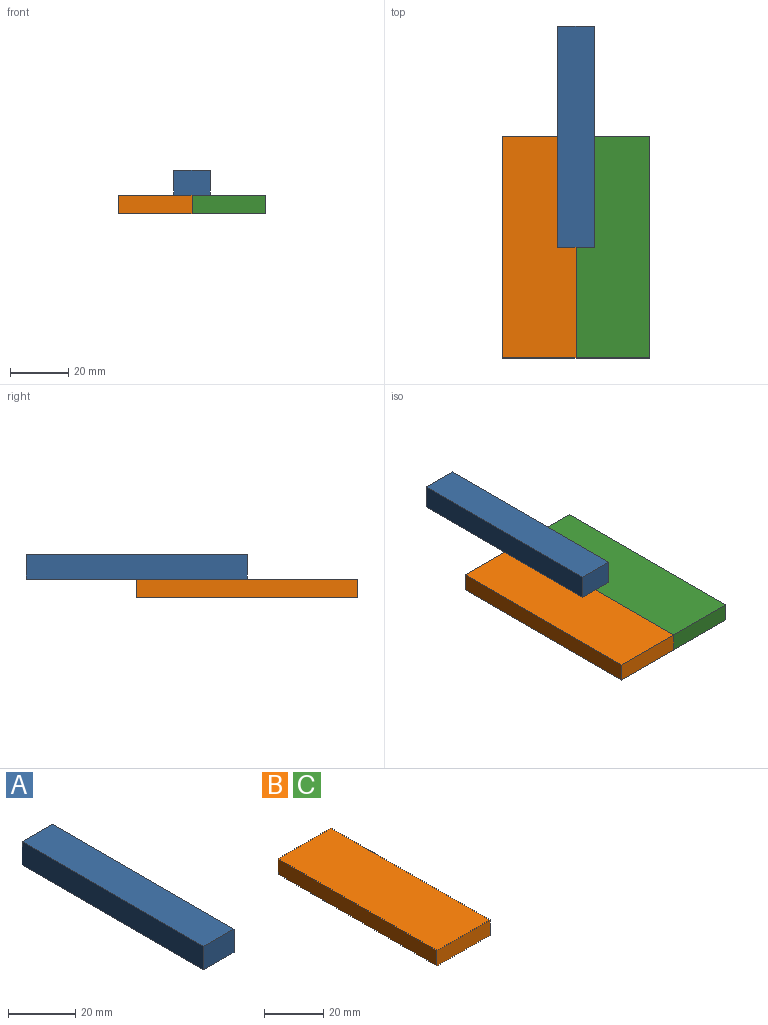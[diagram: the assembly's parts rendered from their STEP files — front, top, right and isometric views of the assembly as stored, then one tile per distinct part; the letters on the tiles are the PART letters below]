
ASSEMBLY  parts=3 mates=2
PART A: 6 faces, bbox 12.7x76.2x8.5 mm
  f0: plane 12.7x8.47mm, normal (0,1,0), area 107.5mm2, adj f1,f3,f4,f5
  f1: plane 76.2x8.47mm, normal (-1,0,0), area 645.2mm2, adj f0,f2,f4,f5
  f2: plane 12.7x8.47mm, normal (0,-1,0), area 107.5mm2, adj f1,f3,f4,f5
  f3: plane 76.2x8.47mm, normal (1,0,0), area 645.2mm2, adj f0,f2,f4,f5
  f4: plane 76.2x12.7mm, normal (0,0,1), area 967.7mm2, adj f0,f1,f2,f3
  f5: plane 76.2x12.7mm, normal (0,0,-1), area 967.7mm2, adj f0,f1,f2,f3
PART B: 6 faces, bbox 25.4x76.2x6.4 mm
  f0: plane 25.4x6.35mm, normal (0,1,0), area 161.3mm2, adj f1,f3,f4,f5
  f1: plane 76.2x6.35mm, normal (-1,0,0), area 483.9mm2, adj f0,f2,f4,f5
  f2: plane 25.4x6.35mm, normal (0,-1,0), area 161.3mm2, adj f1,f3,f4,f5
  f3: plane 76.2x6.35mm, normal (1,0,0), area 483.9mm2, adj f0,f2,f4,f5
  f4: plane 76.2x25.4mm, normal (0,0,1), area 1935.5mm2, adj f0,f1,f2,f3
  f5: plane 76.2x25.4mm, normal (0,0,-1), area 1935.5mm2, adj f0,f1,f2,f3
PART C: same geometry as B
PLACE A t=(29.82,38.1,6.35)mm
PLACE B t=(-25.4,0,0)mm
PLACE C at identity
MATE fastened A.f5 <-> C.f4  axis (0,0,-1) through (-12.7,38.1,6.35)mm
MATE fastened B.f4 <-> A.f5  axis (0,0,1) through (-12.7,38.1,6.35)mm
